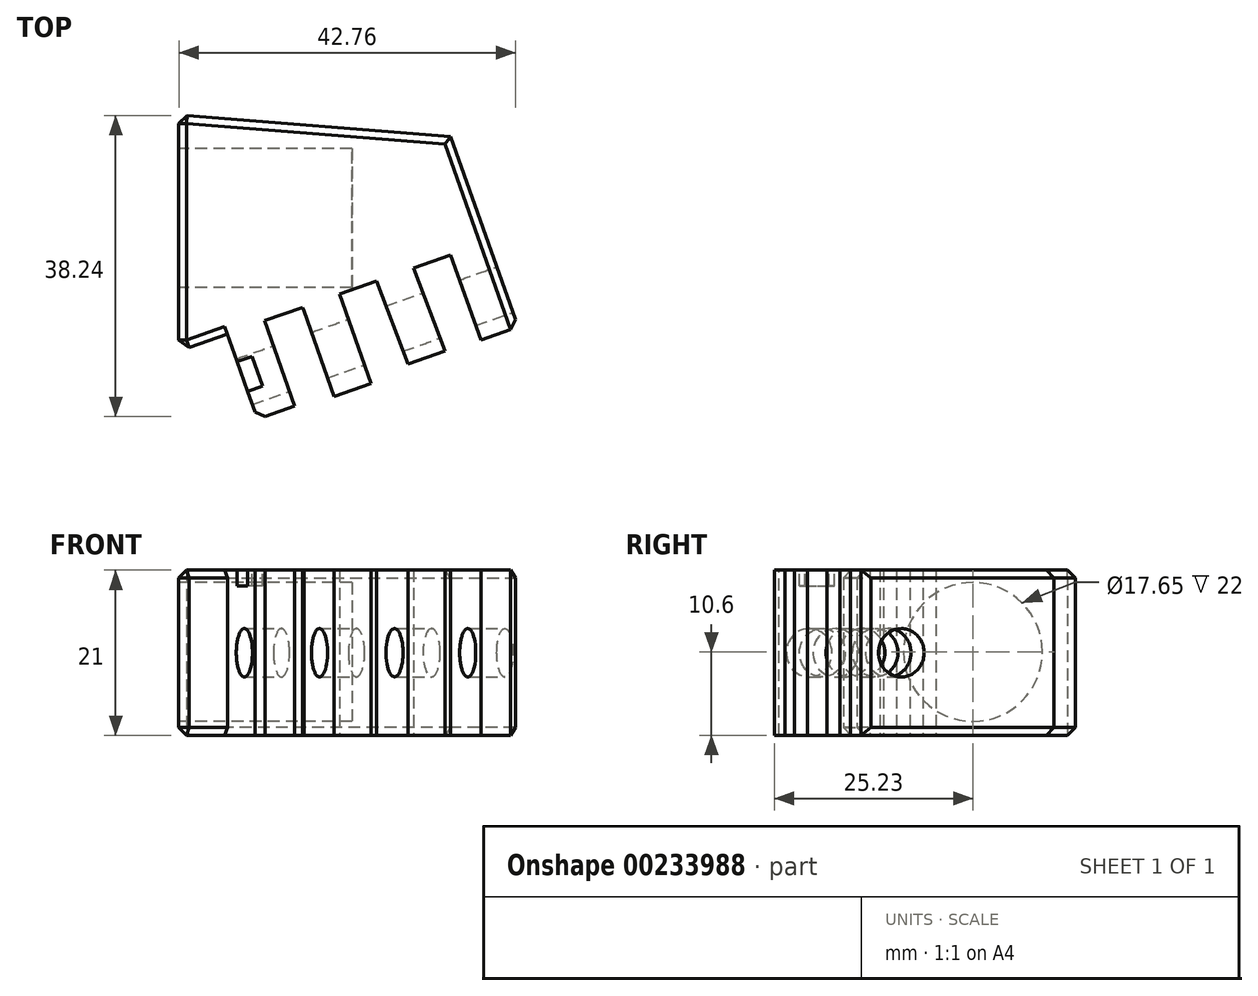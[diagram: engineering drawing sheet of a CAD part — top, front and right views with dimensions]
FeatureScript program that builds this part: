
annotation { "Feature Type Name" : "Feature", "Feature Type Description" : "" }
export const myFeature = defineFeature(function(context is Context, id is Id, definition is map)
    precondition{}
    {
        {
            var Q0;
            Q0=qCreatedBy(makeId("Top.planeOp"),FACE);
            var sketch = newSketch(context, id + "F0", { "sketchPlane" : qUnion([Q0])});
            skLineSegment(sketch, "E0.bottom", {"start": v(-17.27, 16.4) * mm, "end": v(17.27, 13.6) * mm});
            skLineSegment(sketch, "E0.left", {"start": v(-17.27, 16.4) * mm, "end": v(-17.27, -13.6) * mm});
            skPoint(sketch, "E0.middle", {"position": v(0, 0) * mm});
            skLineSegment(sketch, "E1", {"start": v(-17.27, -13.6) * mm, "end": v(17.27, -1.4) * mm});
            skPoint(sketch, "E0.top.end.orphan", {"position": v(17.27, -16.4) * mm});
            skLineSegment(sketch, "E2", {"start": v(17.27, -1.4) * mm, "end": v(21.99, 0.27) * mm});
            skLineSegment(sketch, "E3", {"start": v(17.27, 13.6) * mm, "end": v(21.99, 0.27) * mm});
            skPoint(sketch, "E4.orphan", {"position": v(22.09, 0) * mm});
            skLineSegment(sketch, "E5", {"start": v(-11.1, -11.42) * mm, "end": v(-7.26, -22.27) * mm});
            skLineSegment(sketch, "E6", {"start": v(-7.26, -22.27) * mm, "end": v(-2.55, -20.6) * mm});
            skLineSegment(sketch, "E7", {"start": v(-2.55, -20.6) * mm, "end": v(-6.38, -9.76) * mm});
            skLineSegment(sketch, "E8.1.0.0", {"start": v(3.13, -6.4) * mm, "end": v(3.09, -6.28) * mm});
            skLineSegment(sketch, "E8.1.0.2", {"start": v(-1.56, -8.05) * mm, "end": v(-1.38, -8.54) * mm});
            skLineSegment(sketch, "E8.2.0.0", {"start": v(12.56, -3.06) * mm, "end": v(12.47, -2.83) * mm});
            skLineSegment(sketch, "E8.2.0.2", {"start": v(7.76, -4.5) * mm, "end": v(7.85, -4.73) * mm});
            skPoint(sketch, "E9.orphan", {"position": v(-11.34, 3.45) * mm});
            skPoint(sketch, "E10.orphan", {"position": v(0.18, 21.48) * mm});
            skPoint(sketch, "E11.orphan", {"position": v(11.81, -15.25) * mm});
            skLineSegment(sketch, "E12", {"start": v(-1.38, -8.54) * mm, "end": v(2.45, -19.38) * mm});
            skLineSegment(sketch, "E13", {"start": v(2.45, -19.38) * mm, "end": v(7.16, -17.72) * mm});
            skLineSegment(sketch, "E14", {"start": v(7.16, -17.72) * mm, "end": v(3.13, -6.4) * mm});
            skLineSegment(sketch, "E15", {"start": v(7.85, -4.73) * mm, "end": v(11.81, -15.25) * mm});
            skLineSegment(sketch, "E16", {"start": v(11.81, -15.25) * mm, "end": v(16.52, -13.58) * mm});
            skLineSegment(sketch, "E17", {"start": v(16.52, -13.58) * mm, "end": v(12.56, -3.06) * mm});
            skLineSegment(sketch, "E18", {"start": v(17.27, -1.4) * mm, "end": v(21.1, -12.23) * mm});
            skLineSegment(sketch, "E19", {"start": v(21.1, -12.23) * mm, "end": v(25.82, -10.57) * mm});
            skLineSegment(sketch, "E20", {"start": v(25.82, -10.57) * mm, "end": v(21.99, 0.27) * mm});
            skSolve(sketch);
        }
        {
            var Q0;
            {var subQ0=sQuery(id+"F0.wireOp",EDGE,"E5");Q0=makeQuery(id+"F0.imprint","IMPRINT",FACE,{"disambiguationData":[TD([[makeQuery(id+"F0.imprint","IMPRINT",EDGE,{"derivedFrom":subQ0}),1.0]])]});}
            var Q1;
            {var subQ2=sQuery(id+"F0.wireOp",EDGE,"E8.1.0.2");Q1=makeQuery(id+"F0.imprint","IMPRINT",FACE,{"disambiguationData":[TD([[makeQuery(id+"F0.imprint","IMPRINT",EDGE,{"derivedFrom":subQ2}),1.0]])]});}
            var Q2;
            {var subQ2=sQuery(id+"F0.wireOp",EDGE,"E15");Q2=makeQuery(id+"F0.imprint","IMPRINT",FACE,{"disambiguationData":[TD([[makeQuery(id+"F0.imprint","IMPRINT",EDGE,{"derivedFrom":subQ2}),1.0]])]});}
            var Q3;
            Q3=makeQuery(id+"F0.imprint","IMPRINT",FACE,{"disambiguationData":[TD([[makeQuery(id+"F0.imprint","IMPRINT",EDGE,{"derivedFrom":sQuery(id+"F0.wireOp",EDGE,"E2")}),-1.0]])]});
            var Q4;
            Q4=makeQuery(id+"F0.imprint","IMPRINT",FACE,{"disambiguationData":[TD([[makeQuery(id+"F0.imprint","IMPRINT",EDGE,{"derivedFrom":sQuery(id+"F0.wireOp",EDGE,"E0.bottom")}),-1.0]])]});
            extrude(context, id + "F1", {"entities" : qUnion([Q0, Q1, Q2, Q3, Q4]), "depth" : 21 * mm});
        }
        {
            var Q0;
            Q0=makeQuery(id+"F1.opExtrude","SWEPT_FACE",FACE,{"disambiguationData":[OSD([sQuery(id+"F0.wireOp",EDGE,"E0.left")])]});
            var sketch = newSketch(context, id + "F2", { "sketchPlane" : qUnion([Q0])});
            skCircle(sketch, "E21", {"center": v(-3.3, 10.6) * mm, "radius": 8.82 * mm});
            skPoint(sketch, "E21.centerSnap0", {"position": v(-16.4, 10.5) * mm});
            skSolve(sketch);
        }
        {
            var Q0;
            Q0=makeQuery(id+"F2.imprint","IMPRINT",FACE,{"disambiguationData":[TD([[makeQuery(id+"F2.imprint","IMPRINT",EDGE,{"derivedFrom":sQuery(id+"F2.wireOp",EDGE,"E21")}),1.0]])]});
            extrude(context, id + "F3", {"entities" : qUnion([Q0]), "operationType" : NewBodyOperationType.REMOVE, "oppositeDirection" : true, "depth" : 22 * mm});
        }
        {
            var Q0;
            Q0=makeQuery(id+"F1.opExtrude","SWEPT_FACE",FACE,{"disambiguationData":[OSD([sQuery(id+"F0.wireOp",EDGE,"E3"),sQuery(id+"F0.wireOp",EDGE,"E20")])]});
            var sketch = newSketch(context, id + "F4", { "sketchPlane" : qUnion([Q0])});
            skCircle(sketch, "E22", {"center": v(-13.52, 10.5) * mm, "radius": 3.08 * mm});
            skPoint(sketch, "E22.centerSnap0", {"position": v(-18.57, 10.5) * mm});
            skSolve(sketch);
        }
        {
            var Q0;
            Q0=makeQuery(id+"F4.imprint","IMPRINT",FACE,{"disambiguationData":[TD([[makeQuery(id+"F4.imprint","IMPRINT",EDGE,{"derivedFrom":sQuery(id+"F4.wireOp",EDGE,"E22")}),1.0]])]});
            extrude(context, id + "F5", {"entities" : qUnion([Q0]), "operationType" : NewBodyOperationType.REMOVE, "endBound" : BoundingType.THROUGH_ALL, "oppositeDirection" : true, "depth" : 25 * mm});
        }
        {
            var Q0;
            Q0=makeQuery(id+"F1.opExtrude","SWEPT_FACE",FACE,{"disambiguationData":[OSD([sQuery(id+"F0.wireOp",EDGE,"E5")])]});
            var sketch = newSketch(context, id + "F6", { "sketchPlane" : qUnion([Q0])});
            skLineSegment(sketch, "E23.bottom", {"start": v(14.82, 19) * mm, "end": v(10.82, 19) * mm});
            skPoint(sketch, "E23.middle", {"position": v(12.82, 21) * mm});
            skPoint(sketch, "E23.left.end.orphan", {"position": v(14.82, 23) * mm});
            skPoint(sketch, "E23.right.end.orphan", {"position": v(10.82, 23) * mm});
            skLineSegment(sketch, "E24", {"start": v(10.82, 19) * mm, "end": v(10.82, 21) * mm});
            skLineSegment(sketch, "E25", {"start": v(14.82, 19) * mm, "end": v(14.82, 21) * mm});
            skSolve(sketch);
        }
        {
            var Q0;
            Q0=makeQuery(id+"F6.imprint","IMPRINT",FACE,{"disambiguationData":[TD([[makeQuery(id+"F6.imprint","IMPRINT",EDGE,{"derivedFrom":sQuery(id+"F6.wireOp",EDGE,"E23.bottom")}),-1.0]])]});
            extrude(context, id + "F7", {"entities" : qUnion([Q0]), "operationType" : NewBodyOperationType.REMOVE, "oppositeDirection" : true, "depth" : 2 * mm});
        }
        {
            var Q0;
            Q0=makeQuery(id+"F1.opExtrude","CAP_EDGE",EDGE,{"disambiguationData":[OSD([sQuery(id+"F0.wireOp",EDGE,"E0.bottom")])],"isStart":false});
            var Q1;
            Q1=makeQuery(id+"F1.opExtrude","CAP_EDGE",EDGE,{"disambiguationData":[OSD([sQuery(id+"F0.wireOp",EDGE,"E3"),sQuery(id+"F0.wireOp",EDGE,"E20")])],"isStart":false});
            var Q2;
            Q2=makeQuery(id+"F1.opExtrude","CAP_EDGE",EDGE,{"disambiguationData":[OSD([sQuery(id+"F0.wireOp",EDGE,"E3"),sQuery(id+"F0.wireOp",EDGE,"E20")])],"isStart":true});
            var Q3;
            Q3=makeQuery(id+"F1.opExtrude","CAP_EDGE",EDGE,{"disambiguationData":[OSD([sQuery(id+"F0.wireOp",EDGE,"E0.bottom")])],"isStart":true});
            var Q4;
            Q4=makeQuery(id+"F1.opExtrude","CAP_EDGE",EDGE,{"disambiguationData":[OSD([sQuery(id+"F0.wireOp",EDGE,"E0.left")])],"isStart":false});
            var Q5;
            Q5=makeQuery(id+"F1.opExtrude","SWEPT_EDGE",EDGE,{"disambiguationData":[OSD([sQuery(id+"F0.wireOp",EDGE,"E0.bottom"),sQuery(id+"F0.wireOp",EDGE,"E0.left")])]});
            var Q6;
            Q6=makeQuery(id+"F1.opExtrude","CAP_EDGE",EDGE,{"disambiguationData":[OSD([sQuery(id+"F0.wireOp",EDGE,"E0.left")])],"isStart":true});
            var Q7;
            Q7=makeQuery(id+"F1.opExtrude","SWEPT_EDGE",EDGE,{"disambiguationData":[OSD([sQuery(id+"F0.wireOp",EDGE,"E0.left"),sQuery(id+"F0.wireOp",EDGE,"E1")])]});
            var Q8;
            Q8=makeQuery(id+"F1.opExtrude","SWEPT_EDGE",EDGE,{"disambiguationData":[OSD([sQuery(id+"F0.wireOp",EDGE,"E19"),sQuery(id+"F0.wireOp",EDGE,"E20")])]});
            var Q9;
            Q9=makeQuery(id+"F1.opExtrude","SWEPT_EDGE",EDGE,{"disambiguationData":[OSD([sQuery(id+"F0.wireOp",EDGE,"E5"),sQuery(id+"F0.wireOp",EDGE,"E6")])]});
            var Q10;
            {var subQ0=sQuery(id+"F0.wireOp",EDGE,"E1");Q10=makeQuery(id+"F1.opExtrude","CAP_EDGE",EDGE,{"disambiguationData":[OSD([subQ0]),TDD([makeQuery(id+"F0.imprint","IMPRINT",EDGE,{"disambiguationData":[TD([[makeQuery(id+"F0.imprint","INTERSECT",VERTEX,{"derivedFrom":[sQuery(id+"F0.wireOp",EDGE,"E0.left"),subQ0]}),-1.0]])],"derivedFrom":subQ0})])],"isStart":true});}
            var Q11;
            {var subQ0=sQuery(id+"F0.wireOp",EDGE,"E1");Q11=makeQuery(id+"F1.opExtrude","CAP_EDGE",EDGE,{"disambiguationData":[OSD([subQ0]),TDD([makeQuery(id+"F0.imprint","IMPRINT",EDGE,{"disambiguationData":[TD([[makeQuery(id+"F0.imprint","INTERSECT",VERTEX,{"derivedFrom":[sQuery(id+"F0.wireOp",EDGE,"E0.left"),subQ0]}),-1.0]])],"derivedFrom":subQ0})])],"isStart":false});}
            chamfer(context, id + "F8", {"entities" : qUnion([Q0, Q1, Q2, Q3, Q4, Q5, Q6, Q7, Q8, Q9, Q10, Q11]), "width" : 1 * mm, "tangentPropagation" : true});
        }
    });
